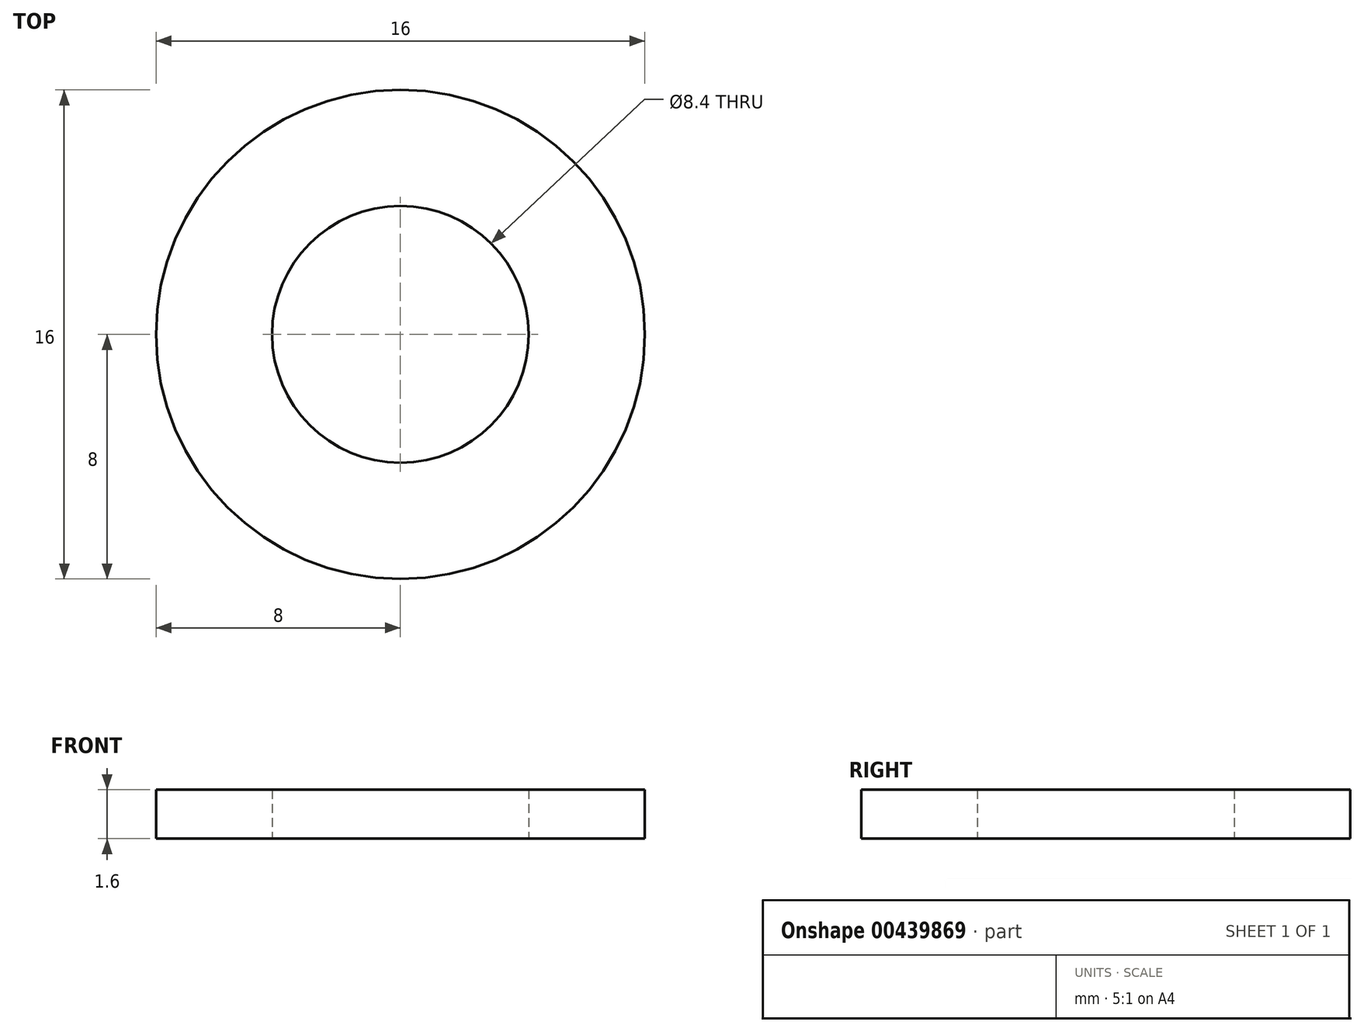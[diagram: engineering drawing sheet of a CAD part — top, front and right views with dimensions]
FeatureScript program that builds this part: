
annotation { "Feature Type Name" : "Feature", "Feature Type Description" : "" }
export const myFeature = defineFeature(function(context is Context, id is Id, definition is map)
    precondition{}
    {
        {
            assignVariable(context, id + "F0", {"name" : "h1", "anyValue" : 1.6});
        }
        {
            var Q0;
            Q0=qCreatedBy(makeId("Top.planeOp"),FACE);
            var sketch = newSketch(context, id + "F1", { "sketchPlane" : qUnion([Q0])});
            skCircle(sketch, "E0", {"center": v(0, 0) * mm, "radius": 4.2 * mm});
            skCircle(sketch, "E1", {"center": v(0, 0) * mm, "radius": 8 * mm});
            skSolve(sketch);
        }
        {
            var Q0;
            Q0=makeQuery(id+"F1.imprint","IMPRINT",FACE,{"disambiguationData":[TD([[makeQuery(id+"F1.imprint","IMPRINT",EDGE,{"derivedFrom":sQuery(id+"F1.wireOp",EDGE,"E0")}),-1.0]])]});
            extrude(context, id + "F2", {"entities" : qUnion([Q0]), "depth" : (getVariable(context, 'h1')) * mm});
        }
    });
